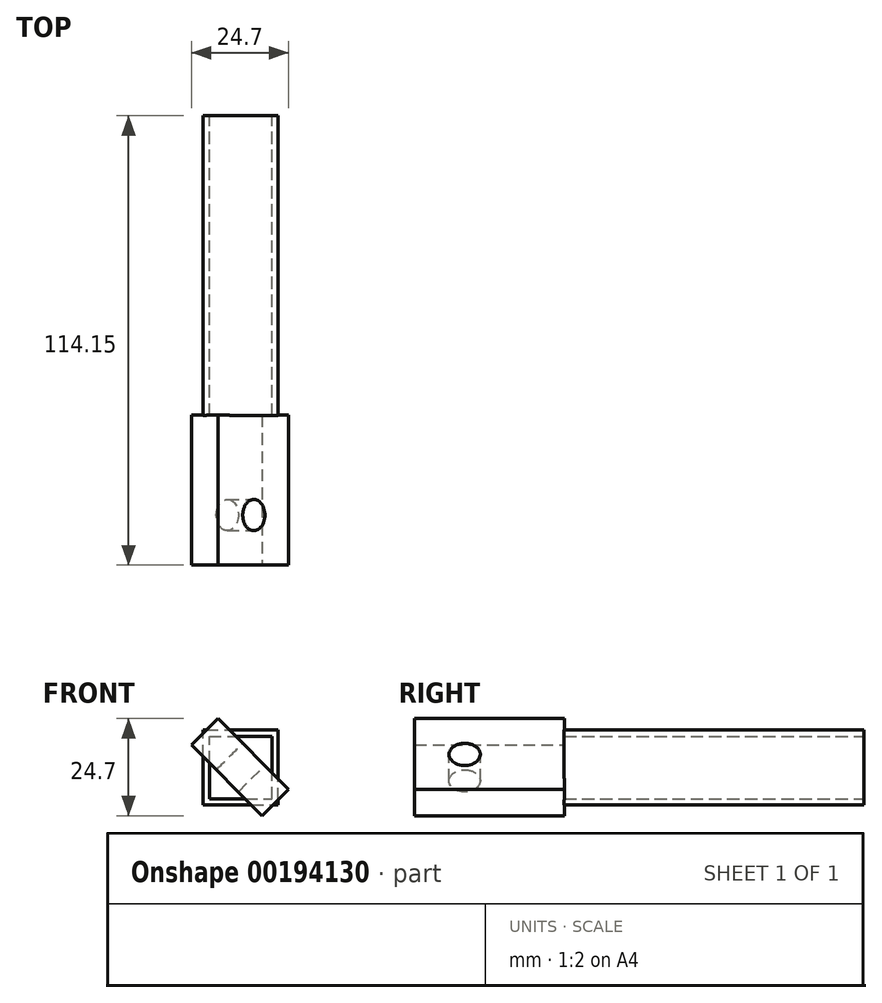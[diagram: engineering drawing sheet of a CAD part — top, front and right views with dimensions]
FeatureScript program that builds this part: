
annotation { "Feature Type Name" : "Feature", "Feature Type Description" : "" }
export const myFeature = defineFeature(function(context is Context, id is Id, definition is map)
    precondition{}
    {
        {
            var Q0;
            Q0=qCreatedBy(makeId("Front.planeOp"),FACE);
            var sketch = newSketch(context, id + "F0", { "sketchPlane" : qUnion([Q0])});
            skLineSegment(sketch, "E0.bottom", {"start": v(0, 0) * mm, "end": v(19.05, 0) * mm});
            skLineSegment(sketch, "E0.top", {"start": v(0, 19.05) * mm, "end": v(19.05, 19.05) * mm});
            skLineSegment(sketch, "E0.left", {"start": v(0, 0) * mm, "end": v(0, 19.05) * mm});
            skLineSegment(sketch, "E0.right", {"start": v(19.05, 0) * mm, "end": v(19.05, 19.05) * mm});
            skLineSegment(sketch, "E1.0", {"start": v(1.59, 1.59) * mm, "end": v(17.46, 1.59) * mm});
            skLineSegment(sketch, "E1.1", {"start": v(1.59, 1.59) * mm, "end": v(1.59, 17.46) * mm});
            skLineSegment(sketch, "E1.2", {"start": v(1.59, 17.46) * mm, "end": v(17.46, 17.46) * mm});
            skLineSegment(sketch, "E1.3", {"start": v(17.46, 1.59) * mm, "end": v(17.46, 17.46) * mm});
            skSolve(sketch);
        }
        {
            var Q0;
            Q0 = qSketchRegion(id + "F0", true);
            extrude(context, id + "F1", {"entities" : qUnion([Q0]), "depth" : 76.2 * mm});
        }
        {
            var Q0;
            Q0=makeQuery(id+"F1.opExtrude","CAP_VERTEX",VERTEX,{"disambiguationData":[OSD([sQuery(id+"F0.wireOp",EDGE,"E0.top"),sQuery(id+"F0.wireOp",EDGE,"E0.left")])],"isStart":false});
            var Q1;
            Q1=makeQuery(id+"F1.opExtrude","CAP_VERTEX",VERTEX,{"disambiguationData":[OSD([sQuery(id+"F0.wireOp",EDGE,"E0.bottom"),sQuery(id+"F0.wireOp",EDGE,"E0.right")])],"isStart":false});
            var Q2;
            Q2=makeQuery(id+"F1.opExtrude","CAP_VERTEX",VERTEX,{"disambiguationData":[OSD([sQuery(id+"F0.wireOp",EDGE,"E0.bottom"),sQuery(id+"F0.wireOp",EDGE,"E0.right")])],"isStart":true});
            cPlane(context, id + "F2", {"entities" : qUnion([Q0, Q1, Q2]), "cplaneType" : CPlaneType.THREE_POINT, "offset" : 25.4 * mm, "width" : 152.4 * mm, "height" : 152.4 * mm});
        }
        {
            var Q0;
            Q0=qCreatedBy(id+"F2.planeOp",FACE);
            var sketch = newSketch(context, id + "F3", { "sketchPlane" : qUnion([Q0])});
            skLineSegment(sketch, "E2", {"start": v(76.05, 12.88) * mm, "end": v(76.05, -12.52) * mm});
            skLineSegment(sketch, "E3", {"start": v(76.05, -12.52) * mm, "end": v(114.15, -12.52) * mm});
            skLineSegment(sketch, "E4", {"start": v(114.15, -12.52) * mm, "end": v(114.15, 12.88) * mm});
            skLineSegment(sketch, "E5", {"start": v(114.15, 12.88) * mm, "end": v(76.05, 12.88) * mm});
            skCircle(sketch, "E6", {"center": v(101.45, 0) * mm, "radius": 3.98 * mm});
            skSolve(sketch);
        }
        {
            var Q0;
            Q0 = qSketchRegion(id + "F3", true);
            extrude(context, id + "F4", {"entities" : qUnion([Q0]), "operationType" : NewBodyOperationType.ADD, "depth" : 4.76 * mm, "hasSecondDirection" : true, "secondDirectionOppositeDirection" : true, "secondDirectionDepth" : 4.76 * mm});
        }
    });
